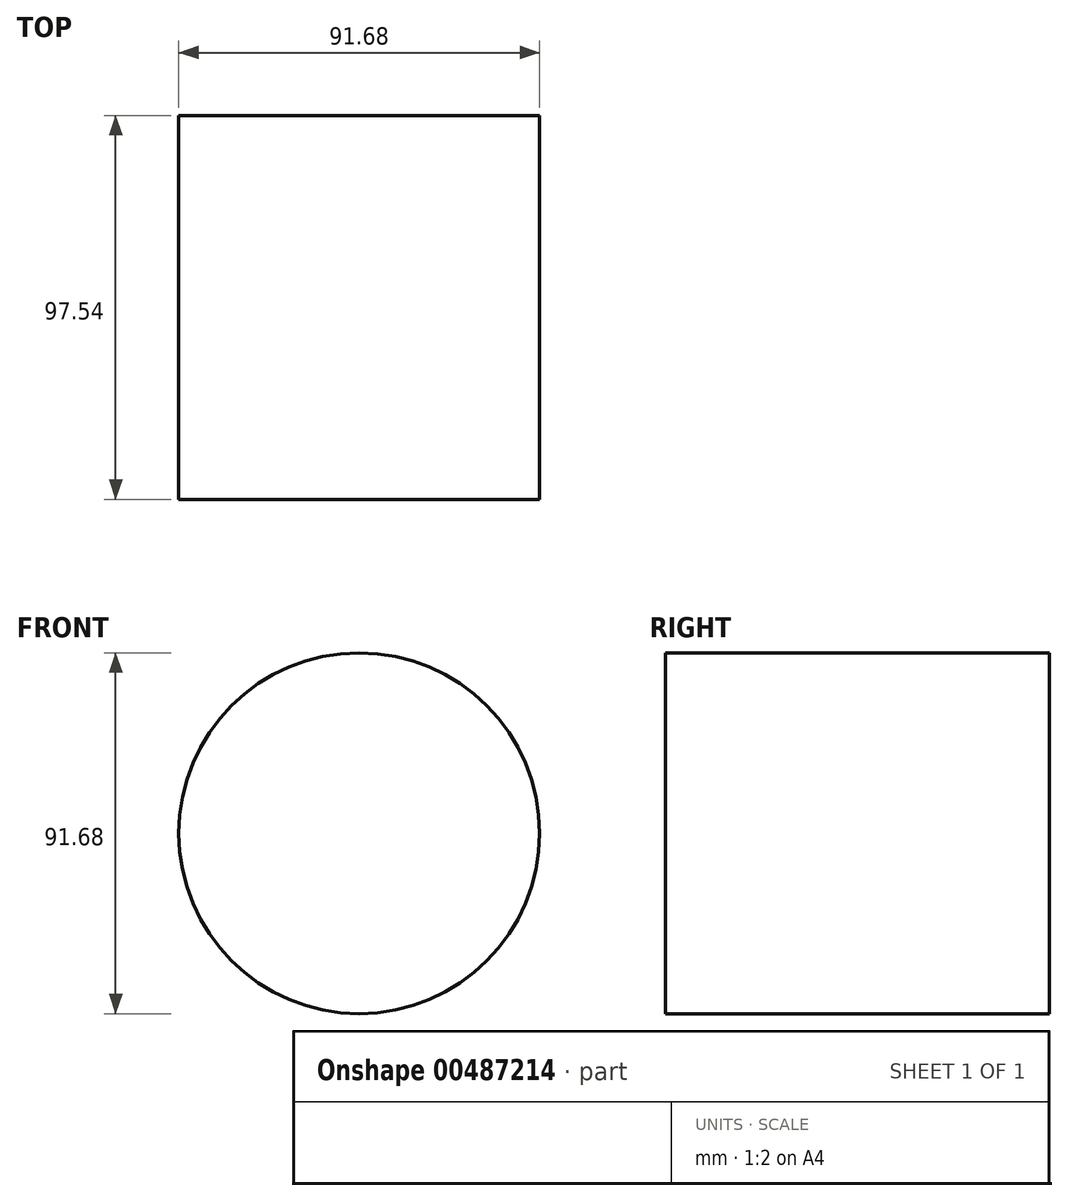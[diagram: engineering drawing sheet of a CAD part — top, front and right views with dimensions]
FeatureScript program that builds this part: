
annotation { "Feature Type Name" : "Feature", "Feature Type Description" : "" }
export const myFeature = defineFeature(function(context is Context, id is Id, definition is map)
    precondition{}
    {
        {
            var Q0;
            Q0=qCreatedBy(makeId("Front.planeOp"),FACE);
            var sketch = newSketch(context, id + "F0", { "sketchPlane" : qUnion([Q0])});
            skCircle(sketch, "E0", {"center": v(0, 0) * mm, "radius": 45.84 * mm});
            skSolve(sketch);
        }
        {
            var Q0;
            Q0=makeQuery(id+"F0.imprint","IMPRINT",FACE,{"disambiguationData":[TD([[makeQuery(id+"F0.imprint","IMPRINT",EDGE,{"derivedFrom":sQuery(id+"F0.wireOp",EDGE,"E0")}),1.0]])]});
            extrude(context, id + "F1", {"entities" : qUnion([Q0]), "depth" : 97.54 * mm});
        }
    });
